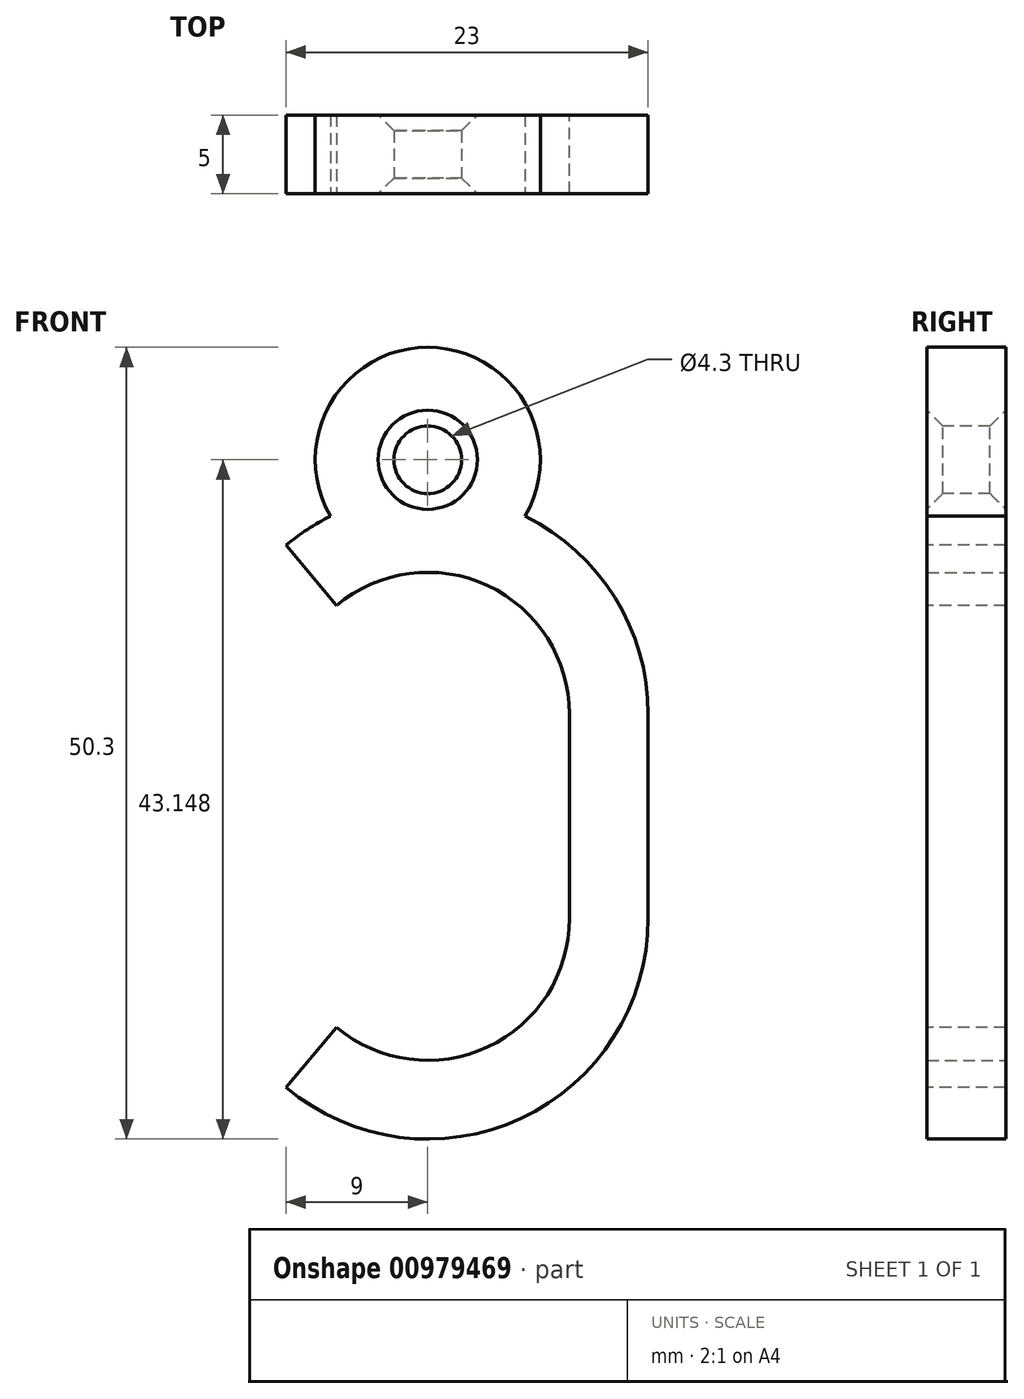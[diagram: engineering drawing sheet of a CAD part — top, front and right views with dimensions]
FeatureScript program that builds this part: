
annotation { "Feature Type Name" : "Feature", "Feature Type Description" : "" }
export const myFeature = defineFeature(function(context is Context, id is Id, definition is map)
    precondition{}
    {
        {
            var Q0;
            Q0=qCreatedBy(makeId("Front.planeOp"),FACE);
            var sketch = newSketch(context, id + "F0", { "sketchPlane" : qUnion([Q0])});
            skLineSegment(sketch, "E0.bottom", {"start": v(9, -6.5) * mm, "end": v(-9, -6.5) * mm});
            skLineSegment(sketch, "E0.top", {"start": v(9, 6.5) * mm, "end": v(-9, 6.5) * mm});
            skLineSegment(sketch, "E0.left", {"start": v(9, -6.5) * mm, "end": v(9, 6.5) * mm});
            skLineSegment(sketch, "E0.right", {"start": v(-9, -6.5) * mm, "end": v(-9, 6.5) * mm});
            skPoint(sketch, "E0.middle", {"position": v(0, 0) * mm});
            skArc(sketch, "E1", {"start": v(9, 6.5) * mm, "mid": v(0, 15.5) * mm, "end": v(-9, 6.5) * mm});
            skArc(sketch, "E2", {"start": v(-9, -6.5) * mm, "mid": v(0, -15.5) * mm, "end": v(9, -6.5) * mm});
            skArc(sketch, "E3.0", {"start": v(14, 6.5) * mm, "mid": v(0, 20.5) * mm, "end": v(-14, 6.5) * mm});
            skLineSegment(sketch, "E3.1", {"start": v(14, -6.5) * mm, "end": v(14, 6.5) * mm});
            skArc(sketch, "E3.2", {"start": v(-14, -6.5) * mm, "mid": v(0, -20.5) * mm, "end": v(14, -6.5) * mm});
            skLineSegment(sketch, "E3.3", {"start": v(-14, -6.5) * mm, "end": v(-14, 6.5) * mm});
            skSolve(sketch);
        }
        {
            var Q0;
            Q0 = qSketchRegion(id + "F0", true);
            extrude(context, id + "F1", {"entities" : qUnion([Q0]), "endBound" : BoundingType.SYMMETRIC, "depth" : 5 * mm, "offsetDistance" : 25 * mm});
        }
        {
            var Q0;
            Q0=makeQuery(id+"F1.opExtrude","CAP_FACE",FACE,{"disambiguationData":[OSD([sQuery(id+"F0.wireOp",EDGE,"E0.left"),sQuery(id+"F0.wireOp",EDGE,"E0.right"),sQuery(id+"F0.wireOp",EDGE,"E1"),sQuery(id+"F0.wireOp",EDGE,"E2"),sQuery(id+"F0.wireOp",EDGE,"E3.0"),sQuery(id+"F0.wireOp",EDGE,"E3.1"),sQuery(id+"F0.wireOp",EDGE,"E3.2"),sQuery(id+"F0.wireOp",EDGE,"E3.3")])],"isStart":false});
            var sketch = newSketch(context, id + "F2", { "sketchPlane" : qUnion([Q0])});
            skLineSegment(sketch, "E4", {"start": v(-9, 6.5) * mm, "end": v(-9, 17.22) * mm, "construction": true});
            skLineSegment(sketch, "E5", {"start": v(-9, -6.5) * mm, "end": v(-9, -17.22) * mm, "construction": true});
            skLineSegment(sketch, "E6", {"start": v(-9, -17.22) * mm, "end": v(-29.52, 0) * mm, "construction": true});
            skLineSegment(sketch, "E7", {"start": v(-29.52, 0) * mm, "end": v(-9, 17.22) * mm, "construction": true});
            skLineSegment(sketch, "E8", {"start": v(-9, 17.22) * mm, "end": v(-5.79, 13.4) * mm});
            skLineSegment(sketch, "E9", {"start": v(-9, -17.22) * mm, "end": v(-5.79, -13.4) * mm});
            skArc(sketch, "E10.0", {"start": v(-5.79, 13.4) * mm, "mid": v(-8.16, 10.3) * mm, "end": v(-9, 6.5) * mm});
            skLineSegment(sketch, "E11.0", {"start": v(-9, -6.5) * mm, "end": v(-9, 6.5) * mm});
            skArc(sketch, "E12.0", {"start": v(-9, -6.5) * mm, "mid": v(-8.16, -10.3) * mm, "end": v(-5.79, -13.4) * mm});
            skArc(sketch, "E13.0", {"start": v(-14, -6.5) * mm, "mid": v(-12.69, -12.42) * mm, "end": v(-9, -17.22) * mm});
            skLineSegment(sketch, "E14.0", {"start": v(-14, -6.5) * mm, "end": v(-14, 6.5) * mm});
            skArc(sketch, "E15.0", {"start": v(-9, 17.22) * mm, "mid": v(-12.69, 12.42) * mm, "end": v(-14, 6.5) * mm});
            skPoint(sketch, "E16.orphan", {"position": v(14, 6.5) * mm});
            skPoint(sketch, "E17.orphan", {"position": v(9, 6.5) * mm});
            skPoint(sketch, "E18.orphan", {"position": v(9, -6.5) * mm});
            skPoint(sketch, "E19.orphan", {"position": v(14, -6.5) * mm});
            skSolve(sketch);
        }
        {
            var Q0;
            Q0 = qSketchRegion(id + "F2", true);
            extrude(context, id + "F3", {"entities" : qUnion([Q0]), "operationType" : NewBodyOperationType.REMOVE, "endBound" : BoundingType.THROUGH_ALL, "oppositeDirection" : true, "depth" : 25 * mm, "offsetDistance" : 25 * mm});
        }
        {
            var Q0;
            Q0=makeQuery(id+"F1.opExtrude","CAP_FACE",FACE,{"disambiguationData":[OSD([sQuery(id+"F0.wireOp",EDGE,"E0.left"),sQuery(id+"F0.wireOp",EDGE,"E0.right"),sQuery(id+"F0.wireOp",EDGE,"E1"),sQuery(id+"F0.wireOp",EDGE,"E2"),sQuery(id+"F0.wireOp",EDGE,"E3.0"),sQuery(id+"F0.wireOp",EDGE,"E3.1"),sQuery(id+"F0.wireOp",EDGE,"E3.2"),sQuery(id+"F0.wireOp",EDGE,"E3.3")])],"isStart":false});
            var sketch = newSketch(context, id + "F4", { "sketchPlane" : qUnion([Q0])});
            skCircle(sketch, "E20", {"center": v(0, 22.65) * mm, "radius": 7.15 * mm});
            skCircle(sketch, "E21", {"center": v(0, 22.65) * mm, "radius": 2.15 * mm});
            skSolve(sketch);
        }
        {
            var Q0;
            Q0 = qSketchRegion(id + "F4", true);
            var Q1;
            Q1=makeQuery(id+"F1.opExtrude","CAP_FACE",FACE,{"disambiguationData":[OSD([sQuery(id+"F0.wireOp",EDGE,"E0.left"),sQuery(id+"F0.wireOp",EDGE,"E0.right"),sQuery(id+"F0.wireOp",EDGE,"E1"),sQuery(id+"F0.wireOp",EDGE,"E2"),sQuery(id+"F0.wireOp",EDGE,"E3.0"),sQuery(id+"F0.wireOp",EDGE,"E3.1"),sQuery(id+"F0.wireOp",EDGE,"E3.2"),sQuery(id+"F0.wireOp",EDGE,"E3.3")])],"isStart":true});
            extrude(context, id + "F5", {"entities" : qUnion([Q0]), "operationType" : NewBodyOperationType.ADD, "endBound" : BoundingType.UP_TO_SURFACE, "oppositeDirection" : true, "depth" : 25 * mm, "endBoundEntityFace" : qUnion([Q1]), "offsetDistance" : 25 * mm});
        }
        {
            var Q0;
            Q0=makeQuery(id+"F5.opExtrude","SWEPT_FACE",FACE,{"disambiguationData":[OSD([sQuery(id+"F4.wireOp",EDGE,"E21")])]});
            chamfer(context, id + "F6", {"entities" : qUnion([Q0]), "width" : 1 * mm, "tangentPropagation" : true});
        }
    });
